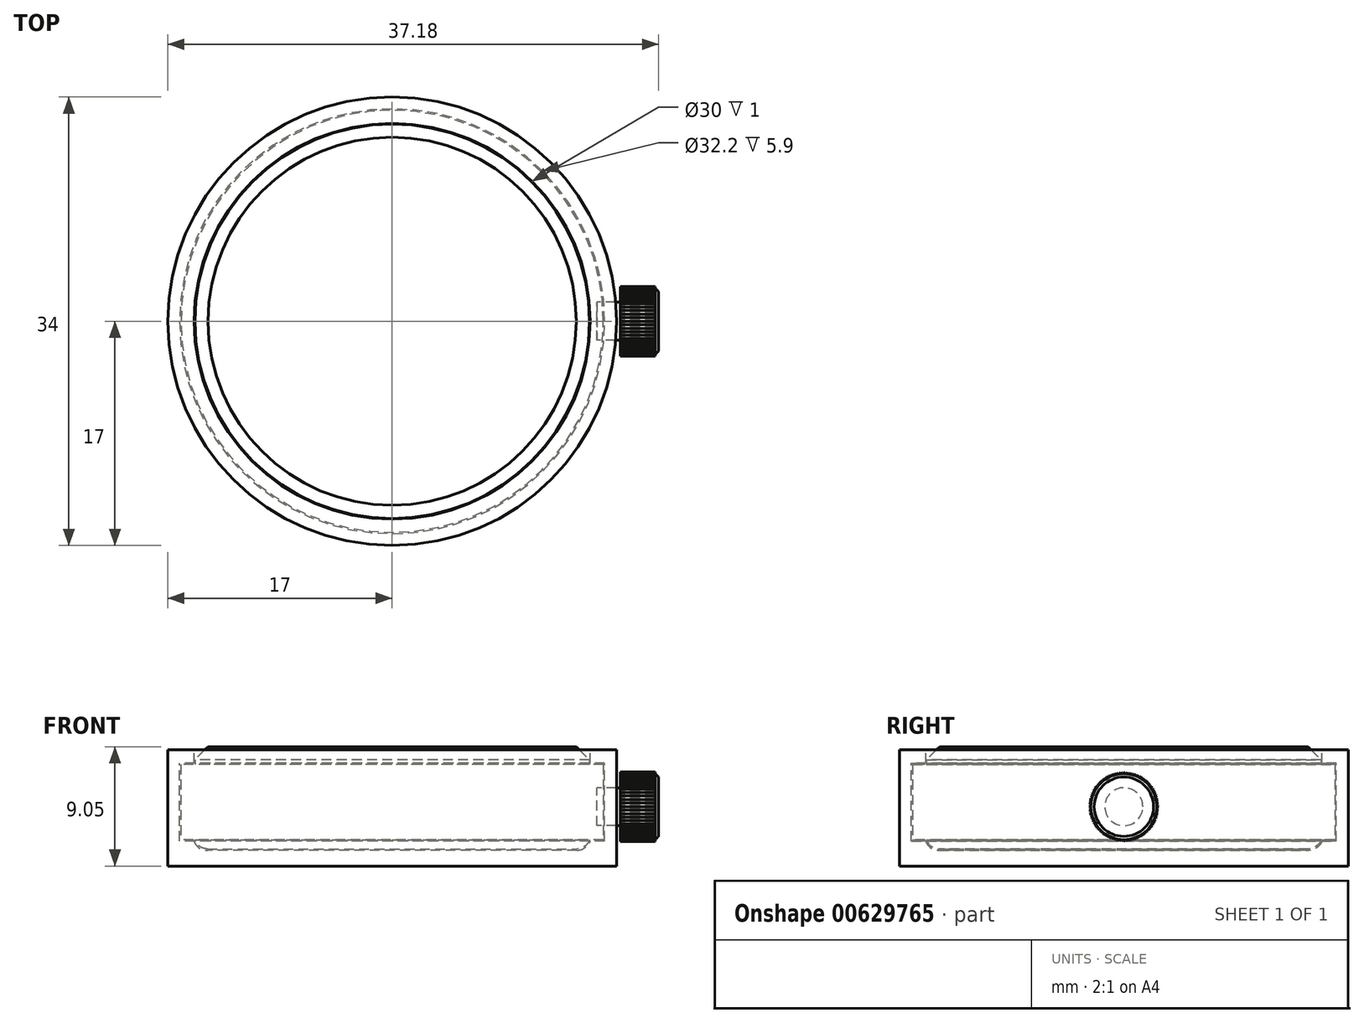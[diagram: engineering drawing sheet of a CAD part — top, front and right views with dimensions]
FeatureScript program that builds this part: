
annotation { "Feature Type Name" : "Feature", "Feature Type Description" : "" }
export const myFeature = defineFeature(function(context is Context, id is Id, definition is map)
    precondition{}
    {
        {
            var Q0;
            Q0=qCreatedBy(makeId("Top.planeOp"),FACE);
            var sketch = newSketch(context, id + "F0", { "sketchPlane" : qUnion([Q0])});
            skCircle(sketch, "E0", {"center": v(0, 0) * mm, "radius": 16 * mm});
            skLineSegment(sketch, "E1", {"start": v(16, 9.79) * mm, "end": v(16, -9.16) * mm, "construction": true});
            skSolve(sketch);
        }
        {
            var Q0;
            Q0=makeQuery(id+"F0.imprint","IMPRINT",FACE,{"disambiguationData":[TD([[makeQuery(id+"F0.imprint","IMPRINT",EDGE,{"derivedFrom":sQuery(id+"F0.wireOp",EDGE,"E0")}),1.0]])]});
            extrude(context, id + "F1", {"entities" : qUnion([Q0]), "depth" : 5.7 * mm, "offsetDistance" : 25 * mm});
        }
        {
            var Q0;
            Q0=makeQuery(id+"F1.opExtrude","CAP_FACE",FACE,{"disambiguationData":[OSD([sQuery(id+"F0.wireOp",EDGE,"E0")])],"isStart":false});
            var sketch = newSketch(context, id + "F2", { "sketchPlane" : qUnion([Q0])});
            skCircle(sketch, "E2", {"center": v(0, 0) * mm, "radius": 14.95 * mm});
            skSolve(sketch);
        }
        {
            var Q0;
            Q0=makeQuery(id+"F2.imprint","IMPRINT",FACE,{"disambiguationData":[TD([[makeQuery(id+"F2.imprint","IMPRINT",EDGE,{"derivedFrom":sQuery(id+"F2.wireOp",EDGE,"E2")}),1.0]])]});
            extrude(context, id + "F3", {"entities" : qUnion([Q0]), "operationType" : NewBodyOperationType.ADD, "depth" : 1.35 * mm, "offsetDistance" : 25 * mm});
        }
        {
            var Q0;
            Q0=makeQuery(id+"F1.opExtrude","CAP_FACE",FACE,{"disambiguationData":[OSD([sQuery(id+"F0.wireOp",EDGE,"E0")])],"isStart":true});
            var sketch = newSketch(context, id + "F4", { "sketchPlane" : qUnion([Q0])});
            skCircle(sketch, "E3", {"center": v(0, 0) * mm, "radius": 14.95 * mm});
            skSolve(sketch);
        }
        {
            var Q0;
            Q0=makeQuery(id+"F4.imprint","IMPRINT",FACE,{"disambiguationData":[TD([[makeQuery(id+"F4.imprint","IMPRINT",EDGE,{"derivedFrom":sQuery(id+"F4.wireOp",EDGE,"E3")}),1.0]])]});
            extrude(context, id + "F5", {"entities" : qUnion([Q0]), "operationType" : NewBodyOperationType.ADD, "depth" : 0.7 * mm, "offsetDistance" : 25 * mm});
        }
        {
            var Q0;
            Q0=qCreatedBy(makeId("Right.planeOp"),FACE);
            var Q1;
            Q1 = qBodyType(qCreatedBy(id + "F7" ,EDGE), BodyType.WIRE);
            cPlane(context, id + "F6", {"entities" : qUnion([Q0, Q1]), "cplaneType" : CPlaneType.OFFSET, "offset" : 15.5 * mm, "width" : 150 * mm, "height" : 150 * mm});
        }
        {
            var Q0;
            Q0=qCreatedBy(id+"F6.planeOp",FACE);
            var sketch = newSketch(context, id + "F7", { "sketchPlane" : qUnion([Q0])});
            skLineSegment(sketch, "E4", {"start": v(-4.74, 5) * mm, "end": v(4.41, 5) * mm, "construction": true});
            skCircle(sketch, "E5", {"center": v(0, 2.5) * mm, "radius": 1.44 * mm});
            skSolve(sketch);
        }
        {
            var Q0;
            Q0=makeQuery(id+"F7.imprint","IMPRINT",FACE,{"disambiguationData":[TD([[makeQuery(id+"F7.imprint","IMPRINT",EDGE,{"derivedFrom":sQuery(id+"F7.wireOp",EDGE,"E5")}),1.0]])]});
            extrude(context, id + "F8", {"entities" : qUnion([Q0]), "depth" : 1.78 * mm, "offsetDistance" : 25 * mm});
        }
        {
            var Q0;
            Q0=makeQuery(id+"F8.opExtrude","CAP_FACE",FACE,{"disambiguationData":[OSD([sQuery(id+"F7.wireOp",EDGE,"E5")])],"isStart":false});
            var sketch = newSketch(context, id + "F9", { "sketchPlane" : qUnion([Q0])});
            skCircle(sketch, "E6", {"center": v(0, 2.5) * mm, "radius": 2.5 * mm});
            skSolve(sketch);
        }
        {
            var Q0;
            Q0 = qSketchRegion(id + "F9", true);
            extrude(context, id + "F10", {"entities" : qUnion([Q0]), "operationType" : NewBodyOperationType.ADD, "depth" : 2.9 * mm, "offsetDistance" : 25 * mm});
        }
        {
            var Q0;
            Q0=makeQuery(id+"F10.opExtrude","CAP_EDGE",EDGE,{"disambiguationData":[OSD([sQuery(id+"F9.wireOp",EDGE,"E6")])],"isStart":false});
            chamfer(context, id + "F11", {"entities" : qUnion([Q0]), "width" : 0.25 * mm, "tangentPropagation" : true});
        }
        {
            var Q0;
            Q0=makeQuery(id+"F3.opExtrude","CAP_EDGE",EDGE,{"disambiguationData":[OSD([sQuery(id+"F2.wireOp",EDGE,"E2")])],"isStart":false});
            chamfer(context, id + "F12", {"entities" : qUnion([Q0]), "width" : 1 * mm, "tangentPropagation" : true});
        }
        {
            var Q0;
            Q0=makeQuery(id+"F5.opExtrude","CAP_EDGE",EDGE,{"disambiguationData":[OSD([sQuery(id+"F4.wireOp",EDGE,"E3")])],"isStart":false});
            fillet(context, id + "F13", {"entities" : qUnion([Q0]), "radius" : 1 * mm, "tangentPropagation" : true, "allowEdgeOverflow" : false});
        }
        {
            var Q0;
            Q0=makeQuery(id+"F10.opExtrude","CAP_FACE",FACE,{"disambiguationData":[OSD([sQuery(id+"F9.wireOp",EDGE,"E6")])],"isStart":true});
            var sketch = newSketch(context, id + "F14", { "sketchPlane" : qUnion([Q0])});
            skCircle(sketch, "E7", {"center": v(0, 2.5) * mm, "radius": 2.48 * mm, "construction": true});
            skLineSegment(sketch, "E8", {"start": v(-2.47, 2.6) * mm, "end": v(-2.62, 2.5) * mm});
            skLineSegment(sketch, "E9", {"start": v(-2.62, 2.5) * mm, "end": v(-2.47, 2.4) * mm});
            skLineSegment(sketch, "E10", {"start": v(-2.47, 2.4) * mm, "end": v(-2.47, 2.6) * mm});
            skSolve(sketch);
        }
        {
            var Q0;
            Q0 = qSketchRegion(id + "F14", true);
            extrude(context, id + "F15", {"entities" : qUnion([Q0]), "oppositeDirection" : true, "depth" : 2.65 * mm, "hasOffset" : true, "offsetDistance" : 2.9 * mm});
        }
        {
            var Q0;
            Q0=makeQuery(id+"F15.opExtrude","SWEPT_BODY",BODY,{"disambiguationData":[OSD([sQuery(id+"F14.wireOp",EDGE,"E8"),sQuery(id+"F14.wireOp",EDGE,"E9"),sQuery(id+"F14.wireOp",EDGE,"E10")])]});
            var Q1;
            Q1=makeQuery(id+"F10.opExtrude","SWEPT_FACE",FACE,{"disambiguationData":[OSD([sQuery(id+"F9.wireOp",EDGE,"E6")])]});
            circularPattern(context, id + "F16", {"entities" : qUnion([Q0]), "axis" : qUnion([Q1]), "angle" : 360 * degree, "instanceCount" : 60, "equalSpace" : true});
        }
        {
            var Q0;
            Q0=qCreatedBy(makeId("Front.planeOp"),FACE);
            var sketch = newSketch(context, id + "F17", { "sketchPlane" : qUnion([Q0])});
            skLineSegment(sketch, "E11", {"start": v(-15, 5.8) * mm, "end": v(-15, 6.8) * mm});
            skLineSegment(sketch, "E12", {"start": v(-15, 6.8) * mm, "end": v(-17, 6.8) * mm});
            skLineSegment(sketch, "E13", {"start": v(-17, 6.8) * mm, "end": v(-17, -2) * mm});
            skLineSegment(sketch, "E14", {"start": v(-17, -2) * mm, "end": v(0, -2) * mm});
            skLineSegment(sketch, "E15", {"start": v(-15, 5.7) * mm, "end": v(-16, 5.7) * mm, "construction": true});
            skLineSegment(sketch, "E16", {"start": v(-16, 5.7) * mm, "end": v(-16, 0) * mm, "construction": true});
            skLineSegment(sketch, "E17", {"start": v(-16, 0) * mm, "end": v(-14.95, 0) * mm, "construction": true});
            skLineSegment(sketch, "E18", {"start": v(-14, -0.7) * mm, "end": v(0, -0.7) * mm, "construction": true});
            skArc(sketch, "E19", {"start": v(-14.95, 0) * mm, "mid": v(-14.59, -0.5) * mm, "end": v(-14, -0.7) * mm, "construction": true});
            skLineSegment(sketch, "E20.0", {"start": v(-15, 5.8) * mm, "end": v(-16.1, 5.8) * mm});
            skLineSegment(sketch, "E21.0", {"start": v(-16.1, 5.8) * mm, "end": v(-16.1, -0.1) * mm});
            skLineSegment(sketch, "E22.0", {"start": v(-16.1, -0.1) * mm, "end": v(-15.02, -0.1) * mm});
            skLineSegment(sketch, "E23.0", {"start": v(-14, -0.8) * mm, "end": v(0, -0.8) * mm});
            skArc(sketch, "E24.0", {"start": v(-15.02, -0.1) * mm, "mid": v(-14.62, -0.6) * mm, "end": v(-14, -0.8) * mm});
            skLineSegment(sketch, "E25", {"start": v(0, -2.45) * mm, "end": v(0, 8.64) * mm, "construction": true});
            skLineSegment(sketch, "E26", {"start": v(0, -0.8) * mm, "end": v(0, -2) * mm});
            skSolve(sketch);
        }
        {
            var Q0;
            Q0=makeQuery(id+"F17.imprint","IMPRINT",FACE,{"disambiguationData":[TD([[makeQuery(id+"F17.imprint","IMPRINT",EDGE,{"derivedFrom":sQuery(id+"F17.wireOp",EDGE,"E11")}),1.0]])]});
            var Q1;
            Q1=sQuery(id+"F17.wireOp",EDGE,"E26");
            revolve(context, id + "F18", {"entities" : qUnion([Q0]), "axis" : qUnion([Q1]), "revolveType" : RevolveType.FULL});
        }
    });
